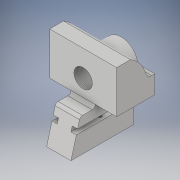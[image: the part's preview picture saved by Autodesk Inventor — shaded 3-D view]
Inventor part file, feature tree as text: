
AUTODESK INVENTOR PART (.ipt)
format: ipt  version: 2017 SP1 (Build 210196100, 196)  size: 212,992 bytes
history: native  units: in
note: dims shown in document units (in); Inventor stores cm internally (conversion verified against a paired STEP export)
features: hole x5, extrude x4, sketch x4
ambient origin geometry x8: Origin, YZ Plane, XZ Plane, XY Plane, X Axis, Y Axis, Z Axis, Center Point
bodies: Solid1 (feature_tree)
feature tree (13):
  extrude  "Extrusion1"  Depth=0.75in
  extrude  "Extrusion2"  Depth=1.1875in
  extrude  "Extrusion3"  Depth=1.375in
  extrude  "Extrusion4"  Depth=2.75in TaperAngle=0.0deg
  hole  "Hole1"  [1 undecoded]
  hole  "Hole2"  [1 undecoded]
  hole  "Hole3"  [1 undecoded]
  hole  "Hole4"  [1 undecoded]
  hole  "Hole5"  [1 undecoded]
  sketch  "Sketch1"  dims[d0=1.75in d1=0.75in]
  sketch  "Sketch2"  dims[d2=1.5625in d3=1.1875in]
  sketch  "Sketch3"  dims[d5=0.125in d6=1.375in]
  sketch  "Sketch5"  dims[d7=0.25in d8=2.75in d9=0.0in d10=1.375in d11=0.875in d13=2.1875in d16=0.875in d17=1.5in d18=0.2175in d19=0.1875in d20=0.5055in d21=2.5625in d22=0.0in d23=1.75in d24=1.0in d25=2.75in d26=0.0in d27=1.375in d28=0.375in d29=0.125in d30=0.125in d31=2.75in d32=0.0in d33=1.188in d34=0.1875in d35=0.1495in d36=0.432in d37=0.142in d38=0.141in d39=90.0deg d40=1.0625in d41=0.0in d42=1.1875in d43=0.1875in d44=0.1495in d45=0.432in d46=0.142in d47=0.141in d48=90.0deg d49=1.0625in d50=0.0in d51=1.0in d52=1.0in d53=0.171in d54=0.432in d55=0.2188in d56=0.375in d57=90.0deg d58=0.75in d59=0.0in d60=1.0in d61=1.0in d62=0.171in d63=0.432in d64=0.2188in d65=0.375in d66=90.0deg d67=0.75in d68=0.0in d69=1.0in d70=1.0in d71=0.758in d72=1.625in d73=0.142in d74=1.1875in d75=90.0deg d76=0.4375in d77=0.0in]
note: 5 required parameter values undecoded (feature->parameter linkage not recoverable at this tier; creation-order binding heuristic only, values carry confidence <= 0.55)
